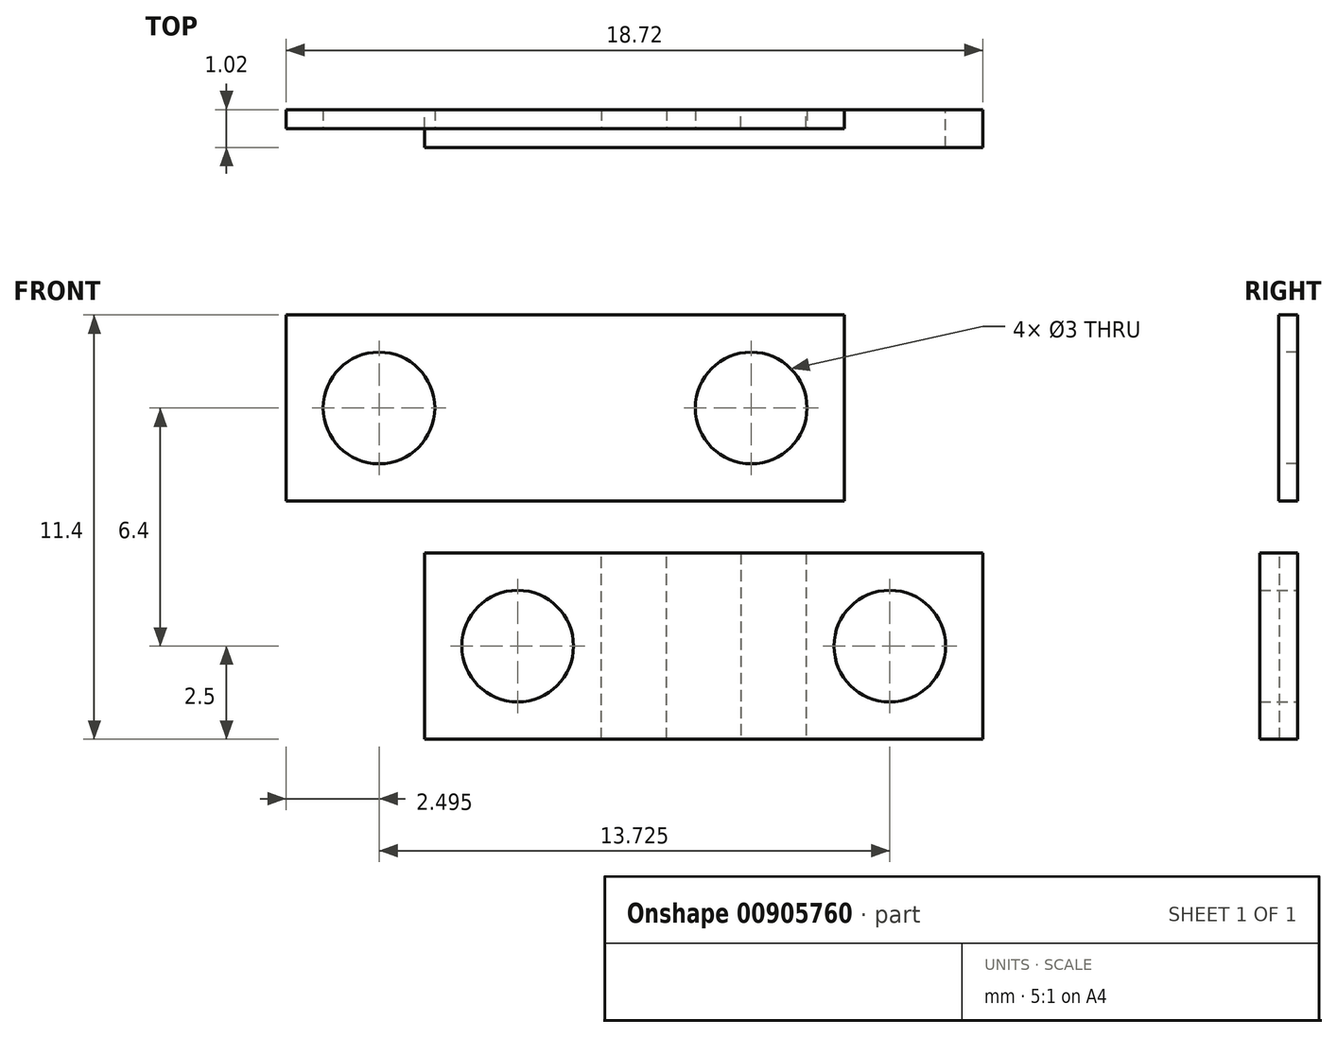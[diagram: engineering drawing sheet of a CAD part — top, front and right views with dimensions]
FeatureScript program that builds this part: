
annotation { "Feature Type Name" : "Feature", "Feature Type Description" : "" }
export const myFeature = defineFeature(function(context is Context, id is Id, definition is map)
    precondition{}
    {
        {
            var Q0;
            Q0=qCreatedBy(makeId("Front.planeOp"),FACE);
            var sketch = newSketch(context, id + "F0", { "sketchPlane" : qUnion([Q0])});
            skLineSegment(sketch, "E0.bottom", {"start": v(-7.5, 2.5) * mm, "end": v(7.5, 2.5) * mm});
            skLineSegment(sketch, "E0.top", {"start": v(-7.5, -2.5) * mm, "end": v(7.5, -2.5) * mm});
            skLineSegment(sketch, "E0.left", {"start": v(-7.5, 2.5) * mm, "end": v(-7.5, -2.5) * mm});
            skLineSegment(sketch, "E0.right", {"start": v(7.5, 2.5) * mm, "end": v(7.5, -2.5) * mm});
            skPoint(sketch, "E0.middle", {"position": v(0, 0) * mm});
            skSolve(sketch);
        }
        {
            var Q0;
            Q0 = qSketchRegion(id + "F0", true);
            extrude(context, id + "F1", {"entities" : qUnion([Q0]), "depth" : 1.02 * mm, "offsetDistance" : 25.4 * mm});
        }
        {
            var Q0;
            Q0=qCreatedBy(makeId("Front.planeOp"),FACE);
            var sketch = newSketch(context, id + "F2", { "sketchPlane" : qUnion([Q0])});
            skLineSegment(sketch, "E1.bottom", {"start": v(3.78, 3.9) * mm, "end": v(-11.22, 3.9) * mm});
            skLineSegment(sketch, "E1.top", {"start": v(3.78, 8.9) * mm, "end": v(-11.22, 8.9) * mm});
            skLineSegment(sketch, "E1.left", {"start": v(3.78, 3.9) * mm, "end": v(3.78, 8.9) * mm});
            skLineSegment(sketch, "E1.right", {"start": v(-11.22, 3.9) * mm, "end": v(-11.22, 8.9) * mm});
            skPoint(sketch, "E1.middle", {"position": v(-3.72, 6.4) * mm});
            skSolve(sketch);
        }
        {
            var Q0;
            Q0=makeQuery(id+"F2.imprint","IMPRINT",FACE,{"disambiguationData":[TD([[makeQuery(id+"F2.imprint","IMPRINT",EDGE,{"derivedFrom":sQuery(id+"F2.wireOp",EDGE,"E1.bottom")}),-1.0]])]});
            extrude(context, id + "F3", {"entities" : qUnion([Q0]), "depth" : 0.5 * mm, "offsetDistance" : 25.4 * mm});
        }
        {
            var Q0;
            Q0=qCreatedBy(makeId("Front.planeOp"),FACE);
            var sketch = newSketch(context, id + "F4", { "sketchPlane" : qUnion([Q0])});
            skLineSegment(sketch, "E2.bottom", {"start": v(-1, -3) * mm, "end": v(-2.75, -3) * mm});
            skLineSegment(sketch, "E2.top", {"start": v(-1, 3) * mm, "end": v(-2.75, 3) * mm});
            skLineSegment(sketch, "E2.left", {"start": v(-1, -3) * mm, "end": v(-1, 3) * mm});
            skLineSegment(sketch, "E2.right", {"start": v(-2.75, -3) * mm, "end": v(-2.75, 3) * mm});
            skPoint(sketch, "E2.middle", {"position": v(-1.88, 0) * mm});
            skSolve(sketch);
        }
        {
            var Q0;
            Q0=makeQuery(id+"F4.imprint","IMPRINT",FACE,{"disambiguationData":[TD([[makeQuery(id+"F4.imprint","IMPRINT",EDGE,{"derivedFrom":sQuery(id+"F4.wireOp",EDGE,"E2.bottom")}),-1.0]])]});
            extrude(context, id + "F5", {"entities" : qUnion([Q0]), "depth" : 0.48 * mm, "offsetDistance" : 25.4 * mm});
        }
        {
            var Q0;
            Q0=qCreatedBy(makeId("Front.planeOp"),FACE);
            var sketch = newSketch(context, id + "F6", { "sketchPlane" : qUnion([Q0])});
            skPoint(sketch, "E3", {"position": v(-5, 0) * mm});
            skPoint(sketch, "E4", {"position": v(5, 0) * mm});
            skSolve(sketch);
        }
        {
            var Q0;
            Q0=sQuery(id+"F6.wireOp",VERTEX,"E3");
            var Q1;
            Q1=sQuery(id+"F6.wireOp",VERTEX,"E4");
            var Q2;
            Q2=makeQuery(id+"F1.opExtrude","SWEPT_BODY",BODY,{"disambiguationData":[OSD([sQuery(id+"F0.wireOp",EDGE,"E0.bottom"),sQuery(id+"F0.wireOp",EDGE,"E0.top"),sQuery(id+"F0.wireOp",EDGE,"E0.left"),sQuery(id+"F0.wireOp",EDGE,"E0.right")])]});
            hole(context, id + "F7", {"style" : HoleStyle.SIMPLE, "endStyle" : HoleEndStyle.THROUGH, "oppositeDirection" : true, "holeDiameter" : 3 * mm, "majorDiameter" : 6.35 * mm, "isTappedThrough" : true, "tappedDepth" : 12.7 * mm, "tapClearance" : 3, "locations" : qUnion([Q0, Q1]), "scope" : qUnion([Q2])});
        }
        {
            var Q0;
            Q0=makeQuery(id+"F5.opExtrude","SWEPT_BODY",BODY,{"disambiguationData":[OSD([sQuery(id+"F4.wireOp",EDGE,"E2.bottom"),sQuery(id+"F4.wireOp",EDGE,"E2.top"),sQuery(id+"F4.wireOp",EDGE,"E2.left"),sQuery(id+"F4.wireOp",EDGE,"E2.right")])]});
            var Q1;
            Q1=makeQuery(id+"F1.opExtrude","SWEPT_BODY",BODY,{"disambiguationData":[OSD([sQuery(id+"F0.wireOp",EDGE,"E0.bottom"),sQuery(id+"F0.wireOp",EDGE,"E0.top"),sQuery(id+"F0.wireOp",EDGE,"E0.left"),sQuery(id+"F0.wireOp",EDGE,"E0.right")])]});
            booleanBodies(context, id + "F8", {"operationType" : BooleanOperationType.SUBTRACTION, "tools" : qUnion([Q0]), "targets" : qUnion([Q1]), "keepTools" : true});
        }
        {
            var Q0;
            Q0=qCreatedBy(makeId("Front.planeOp"),FACE);
            var sketch = newSketch(context, id + "F9", { "sketchPlane" : qUnion([Q0])});
            skLineSegment(sketch, "E5.bottom", {"start": v(1, 3) * mm, "end": v(2.75, 3) * mm});
            skLineSegment(sketch, "E5.top", {"start": v(1, -3) * mm, "end": v(2.75, -3) * mm});
            skLineSegment(sketch, "E5.left", {"start": v(1, 3) * mm, "end": v(1, -3) * mm});
            skLineSegment(sketch, "E5.right", {"start": v(2.75, 3) * mm, "end": v(2.75, -3) * mm});
            skPoint(sketch, "E5.middle", {"position": v(1.88, 0) * mm});
            skSolve(sketch);
        }
        {
            var Q0;
            Q0=makeQuery(id+"F9.imprint","IMPRINT",FACE,{"disambiguationData":[TD([[makeQuery(id+"F9.imprint","IMPRINT",EDGE,{"derivedFrom":sQuery(id+"F9.wireOp",EDGE,"E5.bottom")}),-1.0]])]});
            extrude(context, id + "F10", {"entities" : qUnion([Q0]), "depth" : 0.48 * mm, "offsetDistance" : 25.4 * mm});
        }
        {
            var Q0;
            Q0=makeQuery(id+"F3.opExtrude","CAP_FACE",FACE,{"disambiguationData":[OSD([sQuery(id+"F2.wireOp",EDGE,"E1.bottom"),sQuery(id+"F2.wireOp",EDGE,"E1.top"),sQuery(id+"F2.wireOp",EDGE,"E1.left"),sQuery(id+"F2.wireOp",EDGE,"E1.right")])],"isStart":false});
            var sketch = newSketch(context, id + "F11", { "sketchPlane" : qUnion([Q0])});
            skPoint(sketch, "E6", {"position": v(-8.72, 6.4) * mm});
            skPoint(sketch, "E7", {"position": v(1.28, 6.4) * mm});
            skSolve(sketch);
        }
        {
            var Q0;
            Q0=sQuery(id+"F11.wireOp",VERTEX,"E6");
            var Q1;
            Q1=sQuery(id+"F11.wireOp",VERTEX,"E7");
            var Q2;
            Q2=makeQuery(id+"F3.opExtrude","SWEPT_BODY",BODY,{"disambiguationData":[OSD([sQuery(id+"F2.wireOp",EDGE,"E1.bottom"),sQuery(id+"F2.wireOp",EDGE,"E1.top"),sQuery(id+"F2.wireOp",EDGE,"E1.left"),sQuery(id+"F2.wireOp",EDGE,"E1.right")])]});
            hole(context, id + "F12", {"style" : HoleStyle.SIMPLE, "endStyle" : HoleEndStyle.THROUGH, "holeDiameter" : 3 * mm, "majorDiameter" : 6.35 * mm, "isTappedThrough" : true, "tappedDepth" : 12.7 * mm, "tapClearance" : 3, "locations" : qUnion([Q0, Q1]), "scope" : qUnion([Q2])});
        }
        {
            var Q0;
            Q0=makeQuery(id+"F5.opExtrude","SWEPT_BODY",BODY,{"disambiguationData":[OSD([sQuery(id+"F4.wireOp",EDGE,"E2.bottom"),sQuery(id+"F4.wireOp",EDGE,"E2.top"),sQuery(id+"F4.wireOp",EDGE,"E2.left"),sQuery(id+"F4.wireOp",EDGE,"E2.right")])]});
            var Q1;
            Q1=makeQuery(id+"F10.opExtrude","SWEPT_BODY",BODY,{"disambiguationData":[OSD([sQuery(id+"F9.wireOp",EDGE,"E5.bottom"),sQuery(id+"F9.wireOp",EDGE,"E5.top"),sQuery(id+"F9.wireOp",EDGE,"E5.left"),sQuery(id+"F9.wireOp",EDGE,"E5.right")])]});
            var Q2;
            Q2=makeQuery(id+"F1.opExtrude","SWEPT_BODY",BODY,{"disambiguationData":[OSD([sQuery(id+"F0.wireOp",EDGE,"E0.bottom"),sQuery(id+"F0.wireOp",EDGE,"E0.top"),sQuery(id+"F0.wireOp",EDGE,"E0.left"),sQuery(id+"F0.wireOp",EDGE,"E0.right")])]});
            booleanBodies(context, id + "F13", {"operationType" : BooleanOperationType.SUBTRACTION, "tools" : qUnion([Q0, Q1]), "targets" : qUnion([Q2])});
        }
    });
